# Revit family: Haworth_LC2_LoungeSofas
name_source: partatom
category: Furniture
revit_build: Autodesk Revit 2018 (Build: 20170223_1515(x64)
units: mm (PartAtom-declared; Revit-internal decimal feet)

## family parameters
Always vertical = Yes
Cut with Voids When Loaded = No
OmniClass Number = 23.40.20.00
OmniClass Title = General Furniture and Specialties
Room Calculation Point = No
Shared = No
Work Plane-Based = No

## types (3) — shared parameters
Actual Depth = 2' - 3 3/4"
Actual Height = 2' - 3"
Arm Width = 0' - 6 1/4"
Assembly Code = E2020200
Bench Depth = 1' - 6 11/16"
Bench Height = 1' - 5"
Description = Haworth LC2 Lounge Sofas
Frame Radius = 0' - 0 3/8"
Frame Thickness = 0' - 0 3/4"
Glide Finish = Haworth _ Paint _ Black
Inside Depth = 2' - 2 1/4"
Leg Offset = 0' - 3 5/8"
Manufacturer = Haworth
Model = HCCS-LC2
Revision = 4
Size = Verify Final Dim. w/ Haworth
Three Seat Bar Offset = 0' - 9 1/8"
URL = http://www.haworth.com
URL - Product = http://www.haworth.com
Under Frame Offset = 0' - 1 1/4"
Under Frame Thickness = 0' - 0 1/2"
Warranty = http://www.haworth.com

## per-type parameters (varying)
| type | Actual Width | Cushion Width | End Cushion | Half Width | One Seat | Three Seats | Two Seats | Under Frame |
| HCCS-LC2 - Three Seats | 5' - 10 3/4" | 1' - 6 29/32" | Yes | 2' - 11 3/8" | No | Yes | No | Yes |
| HCCS-LC2 - Two Seats | 4' - 4 1/4" | 1' - 7 1/8" | Yes | 2' - 2 1/8" | No | No | Yes | Yes |
| HCCS-LC2 - One Seat | 2' - 6 9/16" | 1' - 4 9/16" | No | 1' - 3 9/32" | Yes | No | No | No |

## geometry (parser evidence)
native form markers: Sweep x4
no freeform markers — native parametric forms only
